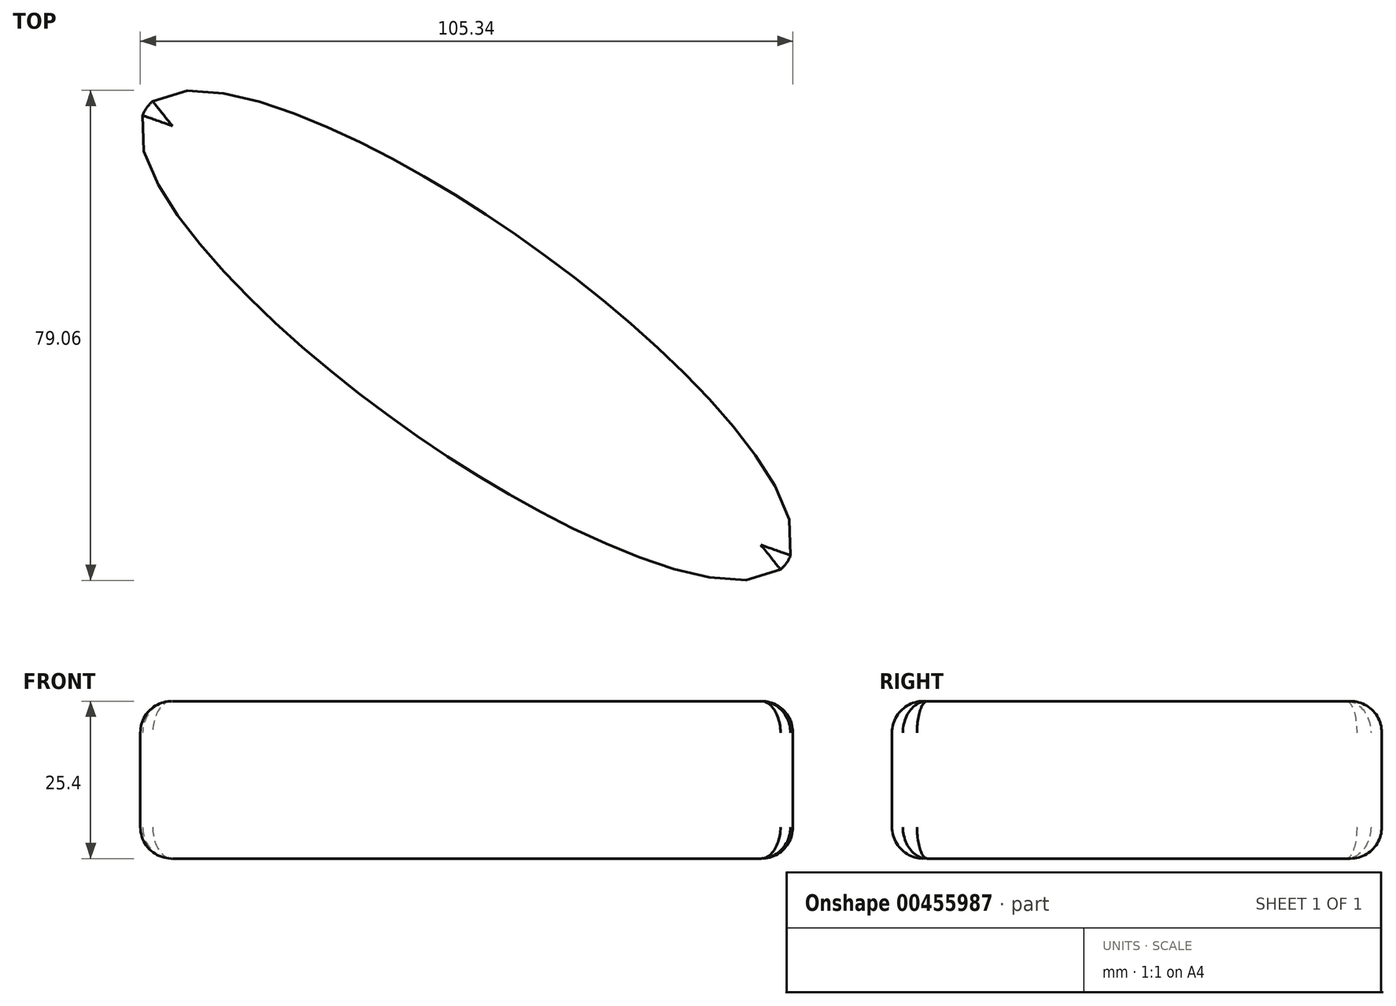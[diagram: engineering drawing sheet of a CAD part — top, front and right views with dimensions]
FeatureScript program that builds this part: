
annotation { "Feature Type Name" : "Feature", "Feature Type Description" : "" }
export const myFeature = defineFeature(function(context is Context, id is Id, definition is map)
    precondition{}
    {
        {
            var Q0;
            Q0=qCreatedBy(makeId("Top.planeOp"),FACE);
            var sketch = newSketch(context, id + "F0", { "sketchPlane" : qUnion([Q0])});
            skEllipse(sketch, "E0", {"center": v(0, 0) * mm, "majorRadius": 63.38 * mm, "minorRadius": 17.88 * mm, "majorAxis": v(0.81, -0.58)});
            skSolve(sketch);
        }
        {
            var Q0;
            Q0 = qSketchRegion(id + "F0", true);
            extrude(context, id + "F1", {"entities" : qUnion([Q0]), "depth" : 25.4 * mm});
        }
        {
            var Q0;
            Q0=makeQuery(id+"F1.opExtrude","SWEPT_FACE",FACE,{"disambiguationData":[OSD([sQuery(id+"F0.wireOp",EDGE,"E0")])]});
            fillet(context, id + "F2", {"entities" : qUnion([Q0]), "radius" : 5.08 * mm, "tangentPropagation" : true, "allowEdgeOverflow" : false});
        }
    });
